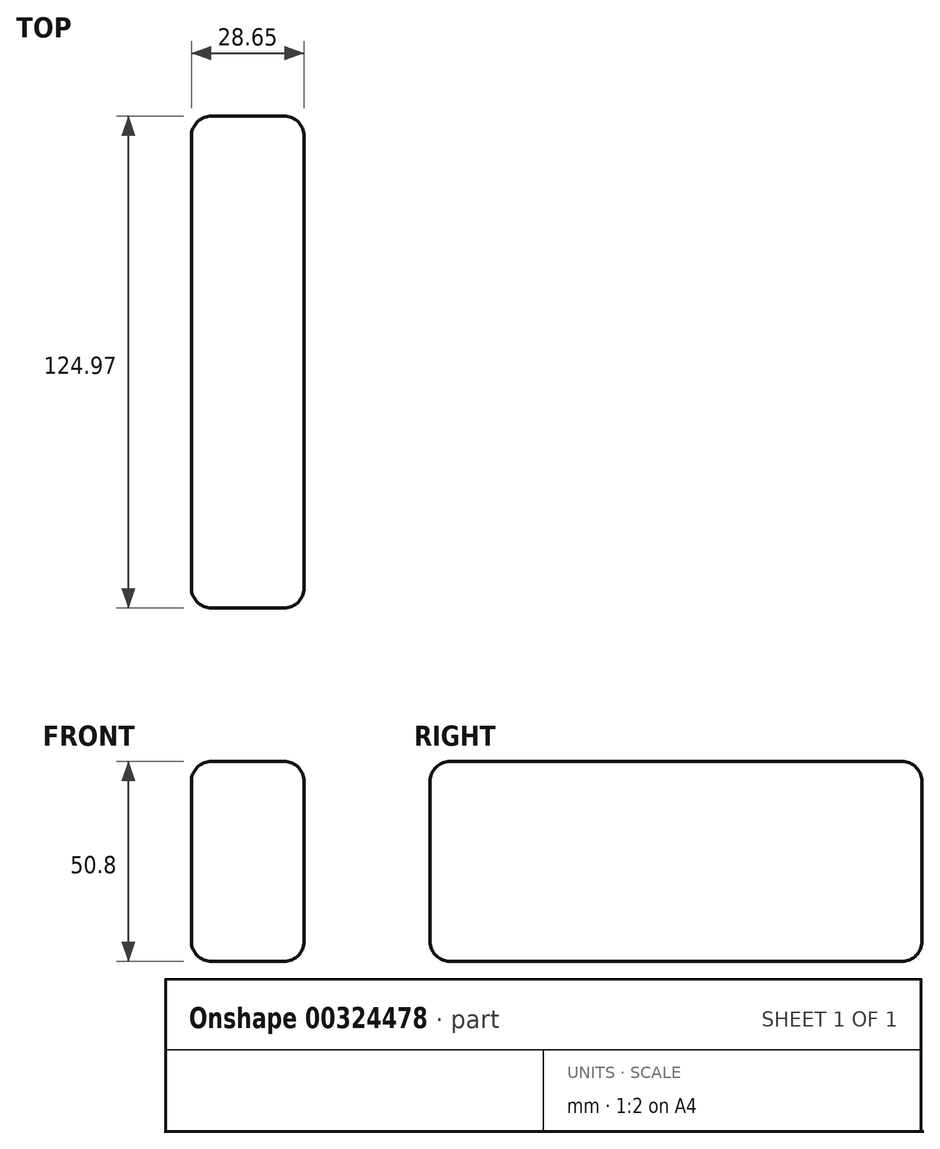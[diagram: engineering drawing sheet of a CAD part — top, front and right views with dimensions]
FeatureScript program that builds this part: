
annotation { "Feature Type Name" : "Feature", "Feature Type Description" : "" }
export const myFeature = defineFeature(function(context is Context, id is Id, definition is map)
    precondition{}
    {
        {
            var Q0;
            Q0=qCreatedBy(makeId("Top.planeOp"),FACE);
            var sketch = newSketch(context, id + "F0", { "sketchPlane" : qUnion([Q0])});
            skLineSegment(sketch, "E0.bottom", {"start": v(-72.85, 63.25) * mm, "end": v(-44.2, 63.25) * mm});
            skLineSegment(sketch, "E0.top", {"start": v(-72.85, -61.72) * mm, "end": v(-44.2, -61.72) * mm});
            skLineSegment(sketch, "E0.left", {"start": v(-72.85, 63.25) * mm, "end": v(-72.85, -61.72) * mm});
            skLineSegment(sketch, "E0.right", {"start": v(-44.2, 63.25) * mm, "end": v(-44.2, -61.72) * mm});
            skSolve(sketch);
        }
        {
            var Q0;
            Q0 = qSketchRegion(id + "F0", true);
            extrude(context, id + "F1", {"entities" : qUnion([Q0]), "depth" : 25.4 * mm, "hasSecondDirection" : true, "secondDirectionOppositeDirection" : true, "secondDirectionDepth" : 25.4 * mm});
        }
        {
            var Q0;
            Q0=makeQuery(id+"F1.opExtrude","CAP_FACE",FACE,{"disambiguationData":[OSD([sQuery(id+"F0.wireOp",EDGE,"E0.bottom"),sQuery(id+"F0.wireOp",EDGE,"E0.top"),sQuery(id+"F0.wireOp",EDGE,"E0.left"),sQuery(id+"F0.wireOp",EDGE,"E0.right")])],"isStart":false});
            var Q1;
            Q1=makeQuery(id+"F1.opExtrude","CAP_FACE",FACE,{"disambiguationData":[OSD([sQuery(id+"F0.wireOp",EDGE,"E0.bottom"),sQuery(id+"F0.wireOp",EDGE,"E0.top"),sQuery(id+"F0.wireOp",EDGE,"E0.left"),sQuery(id+"F0.wireOp",EDGE,"E0.right")])],"isStart":true});
            var Q2;
            Q2=makeQuery(id+"F1.opExtrude","SWEPT_EDGE",EDGE,{"disambiguationData":[OSD([sQuery(id+"F0.wireOp",EDGE,"E0.bottom"),sQuery(id+"F0.wireOp",EDGE,"E0.right")])]});
            var Q3;
            Q3=makeQuery(id+"F1.opExtrude","SWEPT_EDGE",EDGE,{"disambiguationData":[OSD([sQuery(id+"F0.wireOp",EDGE,"E0.top"),sQuery(id+"F0.wireOp",EDGE,"E0.right")])]});
            var Q4;
            Q4=makeQuery(id+"F1.opExtrude","SWEPT_EDGE",EDGE,{"disambiguationData":[OSD([sQuery(id+"F0.wireOp",EDGE,"E0.bottom"),sQuery(id+"F0.wireOp",EDGE,"E0.left")])]});
            var Q5;
            Q5=makeQuery(id+"F1.opExtrude","SWEPT_FACE",FACE,{"disambiguationData":[OSD([sQuery(id+"F0.wireOp",EDGE,"E0.left")])]});
            fillet(context, id + "F2", {"entities" : qUnion([Q0, Q1, Q2, Q3, Q4, Q5]), "radius" : 5.08 * mm, "tangentPropagation" : true, "allowEdgeOverflow" : false});
        }
        {
            var Q0;
            Q0=makeQuery(id+"F1.opExtrude","SWEPT_BODY",BODY,{"disambiguationData":[OSD([sQuery(id+"F0.wireOp",EDGE,"E0.bottom"),sQuery(id+"F0.wireOp",EDGE,"E0.top"),sQuery(id+"F0.wireOp",EDGE,"E0.left"),sQuery(id+"F0.wireOp",EDGE,"E0.right")])]});
            transform(context, id + "F3", {"entities" : qUnion([Q0]), "transformType" : TransformType.TRANSLATION_3D, "dx" : 0 * mm, "dy" : 0 * mm, "dz" : 0 * mm, "makeCopy" : true});
        }
    });
